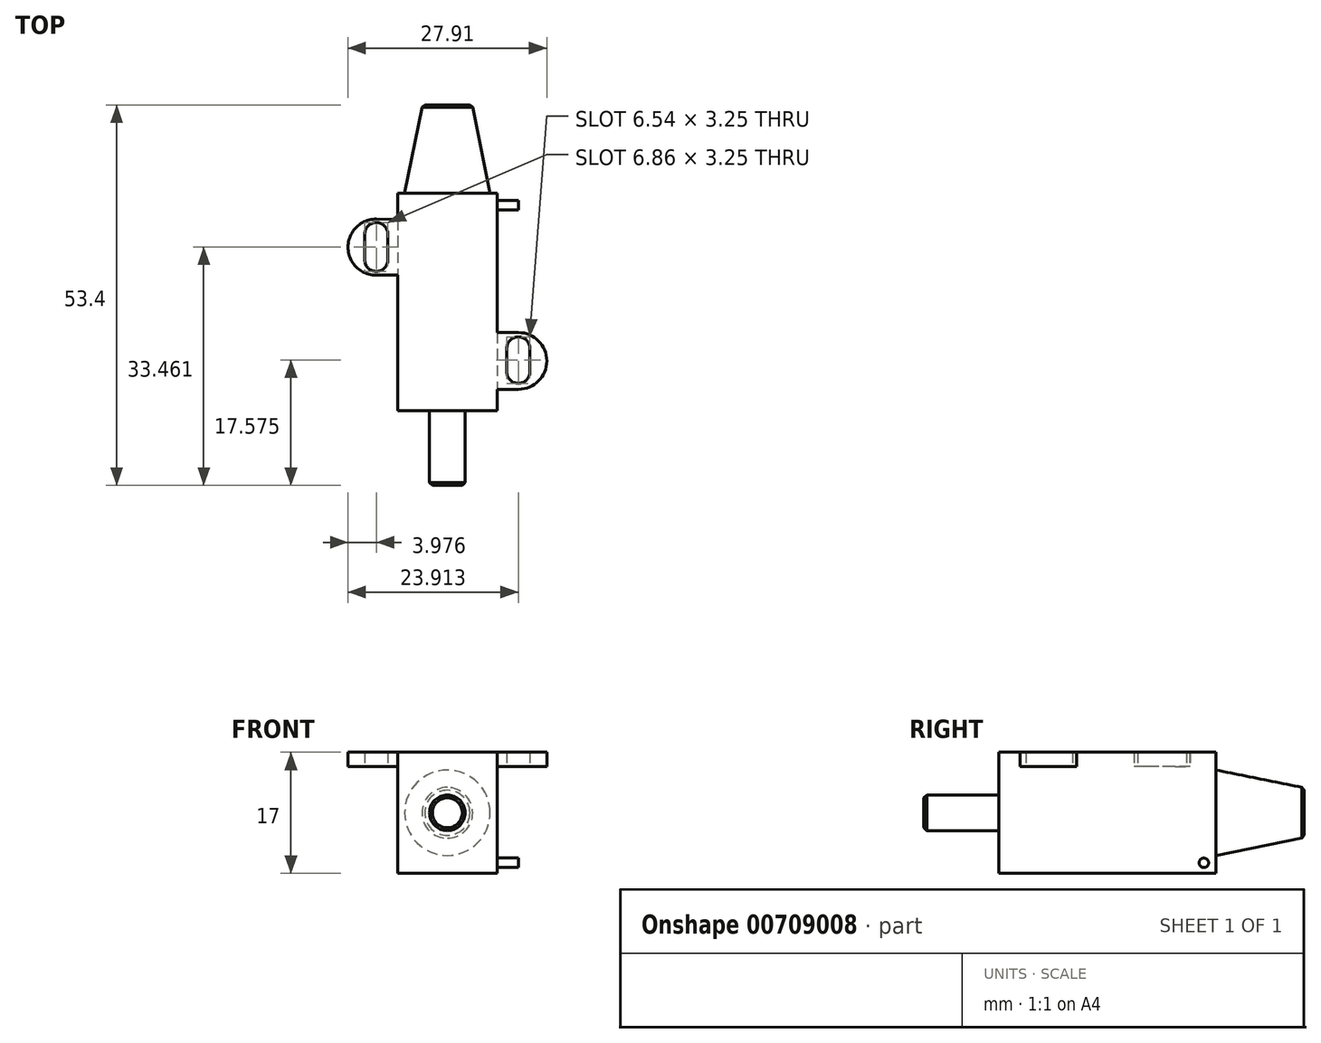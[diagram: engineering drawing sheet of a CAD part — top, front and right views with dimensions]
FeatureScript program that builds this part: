
annotation { "Feature Type Name" : "Feature", "Feature Type Description" : "" }
export const myFeature = defineFeature(function(context is Context, id is Id, definition is map)
    precondition{}
    {
        {
            var Q0;
            Q0=qCreatedBy(makeId("Top.planeOp"),FACE);
            var sketch = newSketch(context, id + "F0", { "sketchPlane" : qUnion([Q0])});
            skLineSegment(sketch, "E0", {"start": v(-12.28, -7.25) * mm, "end": v(-21.78, -7.25) * mm});
            skLineSegment(sketch, "E1", {"start": v(-21.78, -7.25) * mm, "end": v(-21.78, 11.76) * mm});
            skLineSegment(sketch, "E2", {"start": v(-21.78, 11.76) * mm, "end": v(-24.81, 11.76) * mm});
            skArc(sketch, "E3", {"start": v(-24.81, 11.76) * mm, "mid": v(-28.74, 15.72) * mm, "end": v(-24.76, 19.62) * mm});
            skLineSegment(sketch, "E4", {"start": v(-24.76, 19.62) * mm, "end": v(-21.78, 19.57) * mm});
            skLineSegment(sketch, "E5", {"start": v(-21.78, 19.57) * mm, "end": v(-21.78, 23.25) * mm});
            skLineSegment(sketch, "E6", {"start": v(-21.78, 23.25) * mm, "end": v(-7.82, 23.25) * mm});
            skLineSegment(sketch, "E7", {"start": v(-7.82, 23.25) * mm, "end": v(-7.82, 3.69) * mm});
            skLineSegment(sketch, "E8", {"start": v(-7.82, 3.69) * mm, "end": v(-4.8, 3.69) * mm});
            skArc(sketch, "E9", {"start": v(-4.8, 3.69) * mm, "mid": v(-0.83, -0.3) * mm, "end": v(-4.8, -4.28) * mm});
            skLineSegment(sketch, "E10", {"start": v(-4.8, -4.28) * mm, "end": v(-7.82, -4.28) * mm});
            skLineSegment(sketch, "E11", {"start": v(-7.82, -4.28) * mm, "end": v(-7.82, -7.25) * mm});
            skLineSegment(sketch, "E12", {"start": v(-7.82, -7.25) * mm, "end": v(-12.28, -7.25) * mm});
            skLineSegment(sketch, "E13", {"start": v(-26.4, 17.51) * mm, "end": v(-26.4, 13.9) * mm});
            skLineSegment(sketch, "E14", {"start": v(-23.14, 17.51) * mm, "end": v(-23.14, 13.9) * mm});
            skArc(sketch, "E15", {"start": v(-26.4, 17.51) * mm, "mid": v(-24.76, 19.14) * mm, "end": v(-23.14, 17.51) * mm});
            skArc(sketch, "E16", {"start": v(-23.14, 13.9) * mm, "mid": v(-24.76, 12.28) * mm, "end": v(-26.4, 13.9) * mm});
            skLineSegment(sketch, "E17", {"start": v(-6.45, 1.47) * mm, "end": v(-6.45, -1.82) * mm});
            skLineSegment(sketch, "E18", {"start": v(-3.2, 1.47) * mm, "end": v(-3.2, -1.82) * mm});
            skArc(sketch, "E19", {"start": v(-6.45, 1.47) * mm, "mid": v(-4.83, 3.1) * mm, "end": v(-3.2, 1.47) * mm});
            skArc(sketch, "E20", {"start": v(-3.2, -1.82) * mm, "mid": v(-4.83, -3.45) * mm, "end": v(-6.45, -1.82) * mm});
            skSolve(sketch);
        }
        {
            var Q0;
            Q0 = qSketchRegion(id + "F0", true);
            extrude(context, id + "F1", {"entities" : qUnion([Q0]), "depth" : 2 * mm, "offsetDistance" : 25 * mm});
        }
        {
            var Q0;
            Q0=makeQuery(id+"F1.opExtrude","CAP_FACE",FACE,{"disambiguationData":[OSD([sQuery(id+"F0.wireOp",EDGE,"E0"),sQuery(id+"F0.wireOp",EDGE,"E1"),sQuery(id+"F0.wireOp",EDGE,"E2"),sQuery(id+"F0.wireOp",EDGE,"E3"),sQuery(id+"F0.wireOp",EDGE,"E4"),sQuery(id+"F0.wireOp",EDGE,"E5"),sQuery(id+"F0.wireOp",EDGE,"E6"),sQuery(id+"F0.wireOp",EDGE,"E7"),sQuery(id+"F0.wireOp",EDGE,"E8"),sQuery(id+"F0.wireOp",EDGE,"E9"),sQuery(id+"F0.wireOp",EDGE,"E10"),sQuery(id+"F0.wireOp",EDGE,"E11"),sQuery(id+"F0.wireOp",EDGE,"E12"),sQuery(id+"F0.wireOp",EDGE,"E13"),sQuery(id+"F0.wireOp",EDGE,"E14"),sQuery(id+"F0.wireOp",EDGE,"E15"),sQuery(id+"F0.wireOp",EDGE,"E16"),sQuery(id+"F0.wireOp",EDGE,"E17"),sQuery(id+"F0.wireOp",EDGE,"E18"),sQuery(id+"F0.wireOp",EDGE,"E19"),sQuery(id+"F0.wireOp",EDGE,"E20")])],"isStart":false});
            var sketch = newSketch(context, id + "F2", { "sketchPlane" : qUnion([Q0])});
            skLineSegment(sketch, "E21.bottom", {"start": v(-21.78, 23.25) * mm, "end": v(-7.82, 23.25) * mm});
            skLineSegment(sketch, "E21.top", {"start": v(-21.78, -7.25) * mm, "end": v(-7.82, -7.25) * mm});
            skLineSegment(sketch, "E21.left", {"start": v(-21.78, 23.25) * mm, "end": v(-21.78, -7.25) * mm});
            skLineSegment(sketch, "E21.right", {"start": v(-7.82, 23.25) * mm, "end": v(-7.82, -7.25) * mm});
            skSolve(sketch);
        }
        {
            var Q0;
            Q0 = qSketchRegion(id + "F2", true);
            extrude(context, id + "F3", {"entities" : qUnion([Q0]), "operationType" : NewBodyOperationType.ADD, "oppositeDirection" : true, "depth" : 17 * mm, "offsetDistance" : 25 * mm});
        }
        {
            var Q0;
            Q0=makeQuery(id+"F3.boolean.opBoolean","MERGE",FACE,{"derivedFrom":[makeQuery(id+"F1.opExtrude","SWEPT_FACE",FACE,{"disambiguationData":[OSD([sQuery(id+"F0.wireOp",EDGE,"E0"),sQuery(id+"F0.wireOp",EDGE,"E12")])]}),makeQuery(id+"F3.opExtrude","SWEPT_FACE",FACE,{"disambiguationData":[OSD([sQuery(id+"F2.wireOp",EDGE,"E21.top")])]})]});
            var sketch = newSketch(context, id + "F4", { "sketchPlane" : qUnion([Q0])});
            skLineSegment(sketch, "E22", {"start": v(-21.78, -15) * mm, "end": v(-7.82, 2) * mm, "construction": true});
            skLineSegment(sketch, "E23", {"start": v(-7.82, -15) * mm, "end": v(-21.78, 2) * mm, "construction": true});
            skCircle(sketch, "E24", {"center": v(-14.8, -6.5) * mm, "radius": 2.5 * mm});
            skSolve(sketch);
        }
        {
            var Q0;
            Q0 = qSketchRegion(id + "F4", true);
            extrude(context, id + "F5", {"entities" : qUnion([Q0]), "depth" : 10.5 * mm, "offsetDistance" : 25 * mm});
        }
        {
            var Q0;
            Q0=makeQuery(id+"F3.boolean.opBoolean","MERGE",FACE,{"derivedFrom":[makeQuery(id+"F1.opExtrude","SWEPT_FACE",FACE,{"disambiguationData":[OSD([sQuery(id+"F0.wireOp",EDGE,"E6")])]}),makeQuery(id+"F3.opExtrude","SWEPT_FACE",FACE,{"disambiguationData":[OSD([sQuery(id+"F2.wireOp",EDGE,"E21.bottom")])]})]});
            var sketch = newSketch(context, id + "F6", { "sketchPlane" : qUnion([Q0])});
            skLineSegment(sketch, "E25", {"start": v(7.82, -15) * mm, "end": v(21.78, 2) * mm, "construction": true});
            skLineSegment(sketch, "E26", {"start": v(21.78, -15) * mm, "end": v(7.82, 2) * mm, "construction": true});
            skCircle(sketch, "E27", {"center": v(14.8, -6.5) * mm, "radius": 6 * mm});
            skSolve(sketch);
        }
        {
            var Q0;
            Q0 = qSketchRegion(id + "F6", true);
            extrude(context, id + "F7", {"entities" : qUnion([Q0]), "operationType" : NewBodyOperationType.ADD, "depth" : 12.4 * mm, "offsetDistance" : 25 * mm, "hasDraft" : true, "draftAngle" : 11.4 * degree, "draftPullDirection" : true});
        }
        {
            var Q0;
            Q0=makeQuery(id+"F5.opExtrude","CAP_EDGE",EDGE,{"disambiguationData":[OSD([sQuery(id+"F4.wireOp",EDGE,"E24")])],"isStart":false});
            var Q1;
            Q1=makeQuery(id+"F7.opExtrude","CAP_EDGE",EDGE,{"disambiguationData":[OSD([sQuery(id+"F6.wireOp",EDGE,"E27")])],"isStart":false});
            chamfer(context, id + "F8", {"entities" : qUnion([Q0, Q1]), "width" : 0.4 * mm, "tangentPropagation" : true});
        }
        {
            var Q0;
            Q0=makeQuery(id+"F3.boolean.opBoolean","MERGE",FACE,{"derivedFrom":[makeQuery(id+"F1.opExtrude","SWEPT_FACE",FACE,{"disambiguationData":[OSD([sQuery(id+"F0.wireOp",EDGE,"E7")])]}),makeQuery(id+"F1.opExtrude","SWEPT_FACE",FACE,{"disambiguationData":[OSD([sQuery(id+"F0.wireOp",EDGE,"E11")])]}),makeQuery(id+"F3.opExtrude","SWEPT_FACE",FACE,{"disambiguationData":[OSD([sQuery(id+"F2.wireOp",EDGE,"E21.right")])]})]});
            var sketch = newSketch(context, id + "F9", { "sketchPlane" : qUnion([Q0])});
            skCircle(sketch, "E28", {"center": v(21.56, -13.52) * mm, "radius": 0.66 * mm});
            skSolve(sketch);
        }
        {
            var Q0;
            Q0 = qSketchRegion(id + "F9", true);
            extrude(context, id + "F10", {"entities" : qUnion([Q0]), "operationType" : NewBodyOperationType.ADD, "depth" : 3 * mm, "offsetDistance" : 25 * mm});
        }
    });
